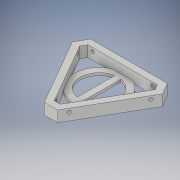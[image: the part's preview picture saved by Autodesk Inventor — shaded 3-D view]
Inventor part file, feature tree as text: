
AUTODESK INVENTOR PART (.ipt)
format: ipt  version: 2018.1 (Build 221171000, 171)  size: 194,560 bytes
history: native  units: mm
features: extrude x5, sketch x4
ambient origin geometry x8: Origin, YZ Plane, XZ Plane, XY Plane, X Axis, Y Axis, Z Axis, Center Point
bodies: Body1 (feature_tree)
feature tree (9):
  sketch  "Sketch1"  dims[d0=100.0mm d7=35.355339mm]
  extrude  "Extrusion5"  Depth=35.355339mm
  sketch  "Sketch5"  dims[d9=12.941mm d10=48.296279mm]
  sketch  "Sketch6"  dims[d11=35.355339mm d12=35.355304mm]
  sketch  "Sketch7"  dims[d13=35.355374mm d17=12.940952mm d18=48.296291mm d20=48.296304mm d21=12.940905mm d22=48.296291mm d23=12.940952mm d99=7.5mm d133=2.5mm d134=15.881861mm d140=15.881895mm d143=15.88187mm d144=90.710713mm d145=90.710748mm d146=90.710713mm d147=35.355304mm d148=20.943982mm d149=20.943915mm d150=7.5mm d153=13.0mm d154=0.0mm d155=4.0mm d156=4.0mm d157=4.0mm d158=10.0mm d159=10.0mm d160=4.0mm d161=4.0mm d162=10.0mm d163=4.0mm d164=10.0mm d165=4.0mm d166=4.0mm d167=4.0mm d168=10.0mm d169=10.0mm d170=7.5mm d171=0.0mm d172=7.5mm d173=0.0mm d174=7.5mm d175=0.0mm d176=55.710763mm d177=7.5mm d178=3.75mm d179=3.75mm d183=60.0mm d184=45.0mm d185=60.0mm d186=3.0mm d187=0.0mm]
  extrude  "Extrusion6"  Depth=48.296279mm
  extrude  "Extrusion7"  Depth=35.355304mm
  extrude  "Extrusion8"  Depth=3.0mm
  extrude  "Extrusion9"  Depth=3.0mm
